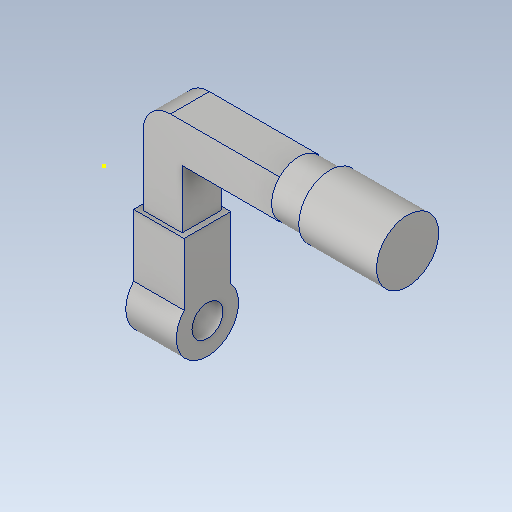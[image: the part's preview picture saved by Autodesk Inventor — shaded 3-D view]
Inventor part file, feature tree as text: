
AUTODESK INVENTOR PART (.ipt)
format: ipt  version: 2021 (Build 250183000, 183)  size: 164,864 bytes
history: native  units: in
note: dims shown in document units (in); Inventor stores cm internally (conversion verified against a paired STEP export)
features: sketch x8, extrude x4, sweep x1, plane x1
ambient origin geometry x8: Origin, YZ Plane, XZ Plane, XY Plane, X Axis, Y Axis, Z Axis, Center Point
bodies: Solid1 (feature_tree)
feature tree (14):
  sketch  "3D Sketch1"
  sweep  "Sweep1"
  sketch  "Sketch2"  dims[d4=3.937in d5=1.9685in]
  extrude  "Extrusion1"  Depth=1.9685in
  extrude  "Extrusion2"  TaperAngle=0.0deg  [1 undecoded]
  extrude  "Extrusion3"  Depth=0.9843in
  extrude  "Extrusion4"  Depth=1.5748in TaperAngle=0.0deg
  sketch  "3D Sketch2"
  plane  "Work Plane1"
  sketch  "Sketch1"  dims[d2=0.3937in d3=5.9055in]
  sketch  "Sketch3"  dims[d6=1.9685in d7=0.0in d8=0.0in]
  sketch  "Sketch4"  dims[d9=2.7559in d10=0.9843in]
  sketch  "Sketch5"  dims[d11=0.9843in d12=1.5748in d13=0.0in]
  sketch  "Sketch6"  dims[d14=3.1496in d15=3.937in d16=0.0in d17=0.9843in d18=0.9843in d19=2.5591in d20=2.3622in d21=3.1496in d22=0.0in d23=1.0417in d24=3.1496in d25=1.5748in d26=2.5591in d27=0.0in]
note: 1 required parameter value undecoded (feature->parameter linkage not recoverable at this tier; creation-order binding heuristic only, values carry confidence <= 0.55)
